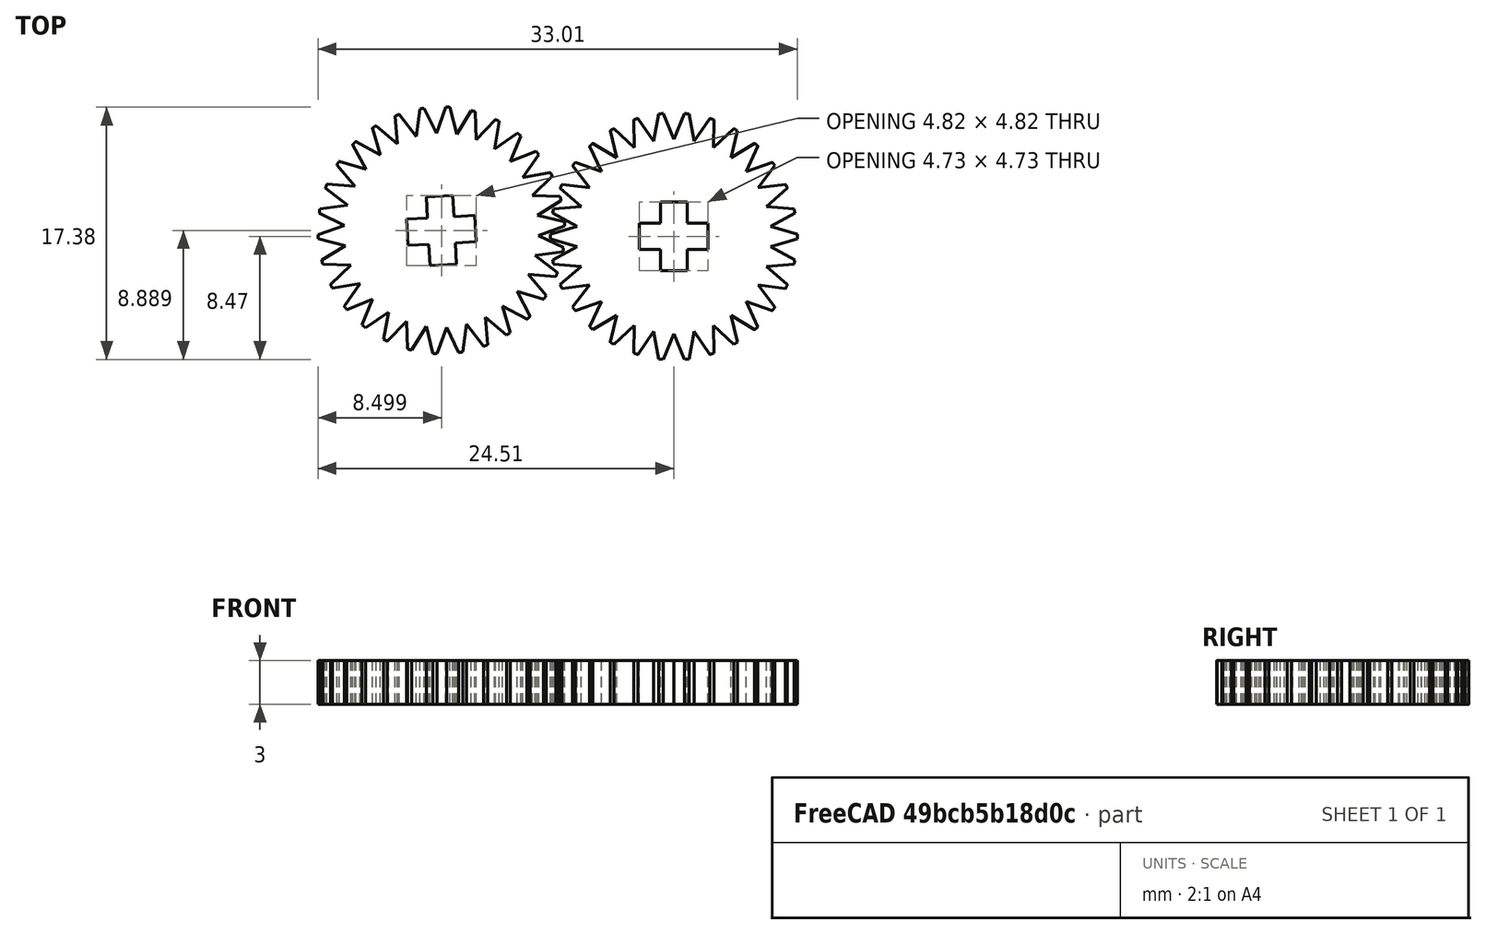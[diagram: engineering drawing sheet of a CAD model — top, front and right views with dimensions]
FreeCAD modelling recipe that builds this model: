
FCSTD DOCUMENT  (FreeCAD 0.18R16117 (Git))
Label: Gear
License: All rights reserved
LicenseURL: http://en.wikipedia.org/wiki/All_rights_reserved
objects: Sketcher::SketchObject×2, PartDesign::Pad×2, PartDesign::Body×2, Part::Cylinder×2, Part::MultiCommon×2
note: 12 computed .brp shape members not serialized (recipe doc carries the construction recipe); baked Part::Feature solids carry a one-line shape summary decoded from their .brp

FEATURE [Sketcher::SketchObject] Sketch
  MapMode = 5
  Support = -> [XY_Plane]
  sketch-geometry (72):
    g0: LineSegment StartX=0.940756 StartY=8.9507 StartZ=0 EndX=1.39301 EndY=6.55359 EndZ=0
    g1: LineSegment StartX=1.39301 StartY=6.55359 StartZ=0 EndX=2.78115 EndY=8.55951 EndZ=0
    g2: LineSegment StartX=2.78115 StartY=8.55951 StartZ=0 EndX=2.72514 EndY=6.12075 EndZ=0
    g3: LineSegment StartX=2.72514 StartY=6.12075 StartZ=0 EndX=4.5 EndY=7.79423 EndZ=0
    g4: LineSegment StartX=4.5 StartY=7.79423 StartZ=0 EndX=3.93816 EndY=5.42041 EndZ=0
    g5: LineSegment StartX=3.93816 StartY=5.42041 StartZ=0 EndX=6.02218 EndY=6.6883 EndZ=0
    g6: LineSegment StartX=6.02218 StartY=6.6883 StartZ=0 EndX=4.97907 EndY=4.48318 EndZ=0
    g7: LineSegment StartX=4.97907 StartY=4.48318 StartZ=0 EndX=7.28115 EndY=5.29007 EndZ=0
    g8: LineSegment StartX=7.28115 StartY=5.29007 StartZ=0 EndX=5.80237 EndY=3.35 EndZ=0
    g9: LineSegment StartX=5.80237 StartY=3.35 StartZ=0 EndX=8.22191 EndY=3.66063 EndZ=0
    g10: LineSegment StartX=8.22191 StartY=3.66063 StartZ=0 EndX=6.37208 EndY=2.07041 EndZ=0
    g11: LineSegment StartX=6.37208 StartY=2.07041 StartZ=0 EndX=8.80333 EndY=1.87121 EndZ=0
    g12: LineSegment StartX=8.80333 StartY=1.87121 StartZ=0 EndX=6.6633 EndY=0.700341 EndZ=0
    g13: LineSegment StartX=6.6633 StartY=0.700341 StartZ=0 EndX=9 EndY=0 EndZ=0
    g14: LineSegment StartX=9 StartY=0 StartZ=0 EndX=6.6633 EndY=-0.700341 EndZ=0
    g15: LineSegment StartX=6.6633 StartY=-0.700341 StartZ=0 EndX=8.80333 EndY=-1.87121 EndZ=0
    g16: LineSegment StartX=8.80333 StartY=-1.87121 StartZ=0 EndX=6.37208 EndY=-2.07041 EndZ=0
    g17: LineSegment StartX=6.37208 StartY=-2.07041 StartZ=0 EndX=8.22191 EndY=-3.66063 EndZ=0
    g18: LineSegment StartX=8.22191 StartY=-3.66063 StartZ=0 EndX=5.80237 EndY=-3.35 EndZ=0
    g19: LineSegment StartX=5.80237 StartY=-3.35 StartZ=0 EndX=7.28115 EndY=-5.29007 EndZ=0
    g20: LineSegment StartX=7.28115 StartY=-5.29007 StartZ=0 EndX=4.97907 EndY=-4.48318 EndZ=0
    g21: LineSegment StartX=4.97907 StartY=-4.48318 StartZ=0 EndX=6.02218 EndY=-6.6883 EndZ=0
    g22: LineSegment StartX=6.02218 StartY=-6.6883 StartZ=0 EndX=3.93816 EndY=-5.42041 EndZ=0
    g23: LineSegment StartX=3.93816 StartY=-5.42041 StartZ=0 EndX=4.5 EndY=-7.79423 EndZ=0
    g24: LineSegment StartX=4.5 StartY=-7.79423 StartZ=0 EndX=2.72514 EndY=-6.12075 EndZ=0
    g25: LineSegment StartX=2.72514 StartY=-6.12075 StartZ=0 EndX=2.78115 EndY=-8.55951 EndZ=0
    g26: LineSegment StartX=2.78115 StartY=-8.55951 StartZ=0 EndX=1.39301 EndY=-6.55359 EndZ=0
    g27: LineSegment StartX=1.39301 StartY=-6.55359 StartZ=0 EndX=0.940756 EndY=-8.9507 EndZ=0
    g28: LineSegment StartX=0.940756 StartY=-8.9507 StartZ=0 EndX=0 EndY=-6.7 EndZ=0
    g29: LineSegment StartX=0 StartY=-6.7 StartZ=0 EndX=-0.940756 EndY=-8.9507 EndZ=0
    g30: LineSegment StartX=-0.940756 StartY=-8.9507 StartZ=0 EndX=-1.39301 EndY=-6.55359 EndZ=0
    g31: LineSegment StartX=-1.39301 StartY=-6.55359 StartZ=0 EndX=-2.78115 EndY=-8.55951 EndZ=0
    g32: LineSegment StartX=-2.78115 StartY=-8.55951 StartZ=0 EndX=-2.72514 EndY=-6.12075 EndZ=0
    g33: LineSegment StartX=-2.72514 StartY=-6.12075 StartZ=0 EndX=-4.5 EndY=-7.79423 EndZ=0
    g34: LineSegment StartX=-4.5 StartY=-7.79423 StartZ=0 EndX=-3.93816 EndY=-5.42041 EndZ=0
    g35: LineSegment StartX=-3.93816 StartY=-5.42041 StartZ=0 EndX=-6.02218 EndY=-6.6883 EndZ=0
    g36: LineSegment StartX=-6.02218 StartY=-6.6883 StartZ=0 EndX=-4.97907 EndY=-4.48318 EndZ=0
    g37: LineSegment StartX=-4.97907 StartY=-4.48318 StartZ=0 EndX=-7.28115 EndY=-5.29007 EndZ=0
    g38: LineSegment StartX=-7.28115 StartY=-5.29007 StartZ=0 EndX=-5.80237 EndY=-3.35 EndZ=0
    g39: LineSegment StartX=-5.80237 StartY=-3.35 StartZ=0 EndX=-8.22191 EndY=-3.66063 EndZ=0
    g40: LineSegment StartX=-8.22191 StartY=-3.66063 StartZ=0 EndX=-6.37208 EndY=-2.07041 EndZ=0
    g41: LineSegment StartX=-6.37208 StartY=-2.07041 StartZ=0 EndX=-8.80333 EndY=-1.87121 EndZ=0
    g42: LineSegment StartX=-8.80333 StartY=-1.87121 StartZ=0 EndX=-6.6633 EndY=-0.700341 EndZ=0
    g43: LineSegment StartX=-6.6633 StartY=-0.700341 StartZ=0 EndX=-9 EndY=7e-15 EndZ=0
    g44: LineSegment StartX=-9 StartY=6.9e-15 StartZ=0 EndX=-6.6633 EndY=0.700341 EndZ=0
    g45: LineSegment StartX=-6.6633 StartY=0.700341 StartZ=0 EndX=-8.80333 EndY=1.87121 EndZ=0
    g46: LineSegment StartX=-8.80333 StartY=1.87121 StartZ=0 EndX=-6.37208 EndY=2.07041 EndZ=0
    g47: LineSegment StartX=-6.37208 StartY=2.07041 StartZ=0 EndX=-8.22191 EndY=3.66063 EndZ=0
    g48: LineSegment StartX=-8.22191 StartY=3.66063 StartZ=0 EndX=-5.80237 EndY=3.35 EndZ=0
    g49: LineSegment StartX=-5.80237 StartY=3.35 StartZ=0 EndX=-7.28115 EndY=5.29007 EndZ=0
    g50: LineSegment StartX=-7.28115 StartY=5.29007 StartZ=0 EndX=-4.97907 EndY=4.48318 EndZ=0
    g51: LineSegment StartX=-4.97907 StartY=4.48318 StartZ=0 EndX=-6.02218 EndY=6.6883 EndZ=0
    g52: LineSegment StartX=-6.02218 StartY=6.6883 StartZ=0 EndX=-3.93816 EndY=5.42041 EndZ=0
    g53: LineSegment StartX=-3.93816 StartY=5.42041 StartZ=0 EndX=-4.5 EndY=7.79423 EndZ=0
    g54: LineSegment StartX=-4.5 StartY=7.79423 StartZ=0 EndX=-2.72514 EndY=6.12075 EndZ=0
    g55: LineSegment StartX=-2.72514 StartY=6.12075 StartZ=0 EndX=-2.78115 EndY=8.55951 EndZ=0
    g56: LineSegment StartX=-2.78115 StartY=8.55951 StartZ=0 EndX=-1.39301 EndY=6.55359 EndZ=0
    g57: LineSegment StartX=-1.39301 StartY=6.55359 StartZ=0 EndX=-0.940756 EndY=8.9507 EndZ=0
    g58: LineSegment StartX=-0.940756 StartY=8.9507 StartZ=0 EndX=1.47e-14 EndY=6.7 EndZ=0
    g59: LineSegment StartX=1.47e-14 StartY=6.7 StartZ=0 EndX=0.940756 EndY=8.9507 EndZ=0
    g60: LineSegment StartX=-2.365 StartY=0.91 StartZ=0 EndX=-0.91 EndY=0.91 EndZ=0
    g61: LineSegment StartX=-0.91 StartY=0.91 StartZ=0 EndX=-0.91 EndY=2.365 EndZ=0
    g62: LineSegment StartX=-0.91 StartY=2.365 StartZ=0 EndX=0.91 EndY=2.365 EndZ=0
    g63: LineSegment StartX=0.91 StartY=2.365 StartZ=0 EndX=0.91 EndY=0.91 EndZ=0
    g64: LineSegment StartX=0.91 StartY=0.91 StartZ=0 EndX=2.365 EndY=0.91 EndZ=0
    g65: LineSegment StartX=2.365 StartY=0.91 StartZ=0 EndX=2.365 EndY=-0.91 EndZ=0
    g66: LineSegment StartX=2.365 StartY=-0.91 StartZ=0 EndX=0.91 EndY=-0.91 EndZ=0
    g67: LineSegment StartX=0.91 StartY=-0.91 StartZ=0 EndX=0.91 EndY=-2.365 EndZ=0
    g68: LineSegment StartX=0.91 StartY=-2.365 StartZ=0 EndX=-0.91 EndY=-2.365 EndZ=0
    g69: LineSegment StartX=-0.91 StartY=-2.365 StartZ=0 EndX=-0.91 EndY=-0.91 EndZ=0
    g70: LineSegment StartX=-0.91 StartY=-0.91 StartZ=0 EndX=-2.365 EndY=-0.91 EndZ=0
    g71: LineSegment StartX=-2.365 StartY=-0.91 StartZ=0 EndX=-2.365 EndY=0.91 EndZ=0
  constraints (96):
    c: Coincident(g0,g1)
    c: Coincident(g1,g2)
    c: Coincident(g2,g3)
    c: Coincident(g3,g4)
    c: Coincident(g4,g5)
    c: Coincident(g5,g6)
    c: Coincident(g6,g7)
    c: Coincident(g7,g8)
    c: Coincident(g8,g9)
    c: Coincident(g9,g10)
    c: Coincident(g10,g11)
    c: Coincident(g11,g12)
    c: Coincident(g12,g13)
    c: Coincident(g13,g14)
    c: Coincident(g14,g15)
    c: Coincident(g15,g16)
    c: Coincident(g16,g17)
    c: Coincident(g17,g18)
    c: Coincident(g18,g19)
    c: Coincident(g19,g20)
    c: Coincident(g20,g21)
    c: Coincident(g21,g22)
    c: Coincident(g22,g23)
    c: Coincident(g23,g24)
    c: Coincident(g24,g25)
    c: Coincident(g25,g26)
    c: Coincident(g26,g27)
    c: Coincident(g27,g28)
    c: Coincident(g28,g29)
    c: Coincident(g29,g30)
    c: Coincident(g30,g31)
    c: Coincident(g31,g32)
    c: Coincident(g32,g33)
    c: Coincident(g33,g34)
    c: Coincident(g34,g35)
    c: Coincident(g35,g36)
    c: Coincident(g36,g37)
    c: Coincident(g37,g38)
    c: Coincident(g38,g39)
    c: Coincident(g39,g40)
    c: Coincident(g40,g41)
    c: Coincident(g41,g42)
    c: Coincident(g42,g43)
    c: Coincident(g43,g44)
    c: Coincident(g44,g45)
    c: Coincident(g45,g46)
    c: Coincident(g46,g47)
    c: Coincident(g47,g48)
    c: Coincident(g48,g49)
    c: Coincident(g49,g50)
    c: Coincident(g50,g51)
    c: Coincident(g51,g52)
    c: Coincident(g52,g53)
    c: Coincident(g53,g54)
    c: Coincident(g54,g55)
    c: Coincident(g55,g56)
    c: Coincident(g56,g57)
    c: Coincident(g57,g58)
    c: Coincident(g58,g59)
    c: Coincident(g59,g0)
    c: Coincident(g60,g61)
    c: Coincident(g61,g62)
    c: Coincident(g62,g63)
    c: Coincident(g63,g64)
    c: Coincident(g64,g65)
    c: Coincident(g65,g66)
    c: Coincident(g66,g67)
    c: Coincident(g67,g68)
    c: Coincident(g68,g69)
    c: Coincident(g69,g70)
    c: Coincident(g70,g71)
    c: Coincident(g60,g71)
    c: Horizontal(g60)
    c: Horizontal(g62)
    c: Horizontal(g64)
    c: Horizontal(g66)
    c: Horizontal(g70)
    c: Vertical(g71)
    c: Vertical(g69)
    c: Vertical(g67)
    c: Vertical(g63)
    c: Vertical(g61)
    c: Equal(g60,g70)
    c: Equal(g70,g61)
    c: Equal(g61,g63)
    c: Equal(g63,g64)
    c: Equal(g64,g66)
    c: Equal(g66,g69)
    c: Equal(g69,g67)
    c: Equal(g62,g65)
    c: Equal(g65,g68)
    c: Equal(g68,g71)
    c: Distance(g65) = 1.82
    c: Distance(g62,g68) = 4.73
    c: DistanceX(g-2,g63) = 0.91
    c: DistanceY(g-1,g66) = -0.91
FEATURE [PartDesign::Pad] Pad
  Length = 3
  Length2 = 100
  Profile = -> Sketch
  Type = 0
FEATURE [PartDesign::Body] Body
  Group = -> [Sketch,Pad]
  Origin = -> Origin
  Placement = pos=(8,0,0) rot=(0,0,1;0rad)
  Tip = -> Pad
FEATURE [Part::Cylinder] Cylinder
  Angle = 360
  AttacherType = Attacher::AttachEngine3D
  Height = 10
  Placement = pos=(8,0,-3.5) rot=(0,0,1;0rad)
  Radius = 8.5
FEATURE [Part::MultiCommon] Common
  Shapes = -> [Cylinder,Body]
FEATURE [Sketcher::SketchObject] Sketch001
  MapMode = 5
  Support = -> [XY_Plane001]
  sketch-geometry (72):
    g0: LineSegment StartX=0.940756 StartY=8.9507 StartZ=0 EndX=1.39301 EndY=6.55359 EndZ=0
    g1: LineSegment StartX=1.39301 StartY=6.55359 StartZ=0 EndX=2.78115 EndY=8.55951 EndZ=0
    g2: LineSegment StartX=2.78115 StartY=8.55951 StartZ=0 EndX=2.72514 EndY=6.12075 EndZ=0
    g3: LineSegment StartX=2.72514 StartY=6.12075 StartZ=0 EndX=4.5 EndY=7.79423 EndZ=0
    g4: LineSegment StartX=4.5 StartY=7.79423 StartZ=0 EndX=3.93816 EndY=5.42041 EndZ=0
    g5: LineSegment StartX=3.93816 StartY=5.42041 StartZ=0 EndX=6.02218 EndY=6.6883 EndZ=0
    g6: LineSegment StartX=6.02218 StartY=6.6883 StartZ=0 EndX=4.97907 EndY=4.48318 EndZ=0
    g7: LineSegment StartX=4.97907 StartY=4.48318 StartZ=0 EndX=7.28115 EndY=5.29007 EndZ=0
    g8: LineSegment StartX=7.28115 StartY=5.29007 StartZ=0 EndX=5.80237 EndY=3.35 EndZ=0
    g9: LineSegment StartX=5.80237 StartY=3.35 StartZ=0 EndX=8.22191 EndY=3.66063 EndZ=0
    g10: LineSegment StartX=8.22191 StartY=3.66063 StartZ=0 EndX=6.37208 EndY=2.07041 EndZ=0
    g11: LineSegment StartX=6.37208 StartY=2.07041 StartZ=0 EndX=8.80333 EndY=1.87121 EndZ=0
    g12: LineSegment StartX=8.80333 StartY=1.87121 StartZ=0 EndX=6.6633 EndY=0.700341 EndZ=0
    g13: LineSegment StartX=6.6633 StartY=0.700341 StartZ=0 EndX=9 EndY=0 EndZ=0
    g14: LineSegment StartX=9 StartY=0 StartZ=0 EndX=6.6633 EndY=-0.700341 EndZ=0
    g15: LineSegment StartX=6.6633 StartY=-0.700341 StartZ=0 EndX=8.80333 EndY=-1.87121 EndZ=0
    g16: LineSegment StartX=8.80333 StartY=-1.87121 StartZ=0 EndX=6.37208 EndY=-2.07041 EndZ=0
    g17: LineSegment StartX=6.37208 StartY=-2.07041 StartZ=0 EndX=8.22191 EndY=-3.66063 EndZ=0
    g18: LineSegment StartX=8.22191 StartY=-3.66063 StartZ=0 EndX=5.80237 EndY=-3.35 EndZ=0
    g19: LineSegment StartX=5.80237 StartY=-3.35 StartZ=0 EndX=7.28115 EndY=-5.29007 EndZ=0
    g20: LineSegment StartX=7.28115 StartY=-5.29007 StartZ=0 EndX=4.97907 EndY=-4.48318 EndZ=0
    g21: LineSegment StartX=4.97907 StartY=-4.48318 StartZ=0 EndX=6.02218 EndY=-6.6883 EndZ=0
    g22: LineSegment StartX=6.02218 StartY=-6.6883 StartZ=0 EndX=3.93816 EndY=-5.42041 EndZ=0
    g23: LineSegment StartX=3.93816 StartY=-5.42041 StartZ=0 EndX=4.5 EndY=-7.79423 EndZ=0
    g24: LineSegment StartX=4.5 StartY=-7.79423 StartZ=0 EndX=2.72514 EndY=-6.12075 EndZ=0
    g25: LineSegment StartX=2.72514 StartY=-6.12075 StartZ=0 EndX=2.78115 EndY=-8.55951 EndZ=0
    g26: LineSegment StartX=2.78115 StartY=-8.55951 StartZ=0 EndX=1.39301 EndY=-6.55359 EndZ=0
    g27: LineSegment StartX=1.39301 StartY=-6.55359 StartZ=0 EndX=0.940756 EndY=-8.9507 EndZ=0
    g28: LineSegment StartX=0.940756 StartY=-8.9507 StartZ=0 EndX=0 EndY=-6.7 EndZ=0
    g29: LineSegment StartX=0 StartY=-6.7 StartZ=0 EndX=-0.940756 EndY=-8.9507 EndZ=0
    g30: LineSegment StartX=-0.940756 StartY=-8.9507 StartZ=0 EndX=-1.39301 EndY=-6.55359 EndZ=0
    g31: LineSegment StartX=-1.39301 StartY=-6.55359 StartZ=0 EndX=-2.78115 EndY=-8.55951 EndZ=0
    g32: LineSegment StartX=-2.78115 StartY=-8.55951 StartZ=0 EndX=-2.72514 EndY=-6.12075 EndZ=0
    g33: LineSegment StartX=-2.72514 StartY=-6.12075 StartZ=0 EndX=-4.5 EndY=-7.79423 EndZ=0
    g34: LineSegment StartX=-4.5 StartY=-7.79423 StartZ=0 EndX=-3.93816 EndY=-5.42041 EndZ=0
    g35: LineSegment StartX=-3.93816 StartY=-5.42041 StartZ=0 EndX=-6.02218 EndY=-6.6883 EndZ=0
    g36: LineSegment StartX=-6.02218 StartY=-6.6883 StartZ=0 EndX=-4.97907 EndY=-4.48318 EndZ=0
    g37: LineSegment StartX=-4.97907 StartY=-4.48318 StartZ=0 EndX=-7.28115 EndY=-5.29007 EndZ=0
    g38: LineSegment StartX=-7.28115 StartY=-5.29007 StartZ=0 EndX=-5.80237 EndY=-3.35 EndZ=0
    g39: LineSegment StartX=-5.80237 StartY=-3.35 StartZ=0 EndX=-8.22191 EndY=-3.66063 EndZ=0
    g40: LineSegment StartX=-8.22191 StartY=-3.66063 StartZ=0 EndX=-6.37208 EndY=-2.07041 EndZ=0
    g41: LineSegment StartX=-6.37208 StartY=-2.07041 StartZ=0 EndX=-8.80333 EndY=-1.87121 EndZ=0
    g42: LineSegment StartX=-8.80333 StartY=-1.87121 StartZ=0 EndX=-6.6633 EndY=-0.700341 EndZ=0
    g43: LineSegment StartX=-6.6633 StartY=-0.700341 StartZ=0 EndX=-9 EndY=6.9e-15 EndZ=0
    g44: LineSegment StartX=-9 StartY=6.9e-15 StartZ=0 EndX=-6.6633 EndY=0.700341 EndZ=0
    g45: LineSegment StartX=-6.6633 StartY=0.700341 StartZ=0 EndX=-8.80333 EndY=1.87121 EndZ=0
    g46: LineSegment StartX=-8.80333 StartY=1.87121 StartZ=0 EndX=-6.37208 EndY=2.07041 EndZ=0
    g47: LineSegment StartX=-6.37208 StartY=2.07041 StartZ=0 EndX=-8.22191 EndY=3.66063 EndZ=0
    g48: LineSegment StartX=-8.22191 StartY=3.66063 StartZ=0 EndX=-5.80237 EndY=3.35 EndZ=0
    g49: LineSegment StartX=-5.80237 StartY=3.35 StartZ=0 EndX=-7.28115 EndY=5.29007 EndZ=0
    g50: LineSegment StartX=-7.28115 StartY=5.29007 StartZ=0 EndX=-4.97907 EndY=4.48318 EndZ=0
    g51: LineSegment StartX=-4.97907 StartY=4.48318 StartZ=0 EndX=-6.02218 EndY=6.6883 EndZ=0
    g52: LineSegment StartX=-6.02218 StartY=6.6883 StartZ=0 EndX=-3.93816 EndY=5.42041 EndZ=0
    g53: LineSegment StartX=-3.93816 StartY=5.42041 StartZ=0 EndX=-4.5 EndY=7.79423 EndZ=0
    g54: LineSegment StartX=-4.5 StartY=7.79423 StartZ=0 EndX=-2.72514 EndY=6.12075 EndZ=0
    g55: LineSegment StartX=-2.72514 StartY=6.12075 StartZ=0 EndX=-2.78115 EndY=8.55951 EndZ=0
    g56: LineSegment StartX=-2.78115 StartY=8.55951 StartZ=0 EndX=-1.39301 EndY=6.55359 EndZ=0
    g57: LineSegment StartX=-1.39301 StartY=6.55359 StartZ=0 EndX=-0.940756 EndY=8.9507 EndZ=0
    g58: LineSegment StartX=-0.940756 StartY=8.9507 StartZ=0 EndX=1.47e-14 EndY=6.7 EndZ=0
    g59: LineSegment StartX=1.47e-14 StartY=6.7 StartZ=0 EndX=0.940756 EndY=8.9507 EndZ=0
    g60: LineSegment StartX=-2.365 StartY=0.91 StartZ=0 EndX=-0.91 EndY=0.91 EndZ=0
    g61: LineSegment StartX=-0.91 StartY=0.91 StartZ=0 EndX=-0.91 EndY=2.365 EndZ=0
    g62: LineSegment StartX=-0.91 StartY=2.365 StartZ=0 EndX=0.91 EndY=2.365 EndZ=0
    g63: LineSegment StartX=0.91 StartY=2.365 StartZ=0 EndX=0.91 EndY=0.91 EndZ=0
    g64: LineSegment StartX=0.91 StartY=0.91 StartZ=0 EndX=2.365 EndY=0.91 EndZ=0
    g65: LineSegment StartX=2.365 StartY=0.91 StartZ=0 EndX=2.365 EndY=-0.91 EndZ=0
    g66: LineSegment StartX=2.365 StartY=-0.91 StartZ=0 EndX=0.91 EndY=-0.91 EndZ=0
    g67: LineSegment StartX=0.91 StartY=-0.91 StartZ=0 EndX=0.91 EndY=-2.365 EndZ=0
    g68: LineSegment StartX=0.91 StartY=-2.365 StartZ=0 EndX=-0.91 EndY=-2.365 EndZ=0
    g69: LineSegment StartX=-0.91 StartY=-2.365 StartZ=0 EndX=-0.91 EndY=-0.91 EndZ=0
    g70: LineSegment StartX=-0.91 StartY=-0.91 StartZ=0 EndX=-2.365 EndY=-0.91 EndZ=0
    g71: LineSegment StartX=-2.365 StartY=-0.91 StartZ=0 EndX=-2.365 EndY=0.91 EndZ=0
  constraints (96):
    c: Coincident(g0,g1)
    c: Coincident(g1,g2)
    c: Coincident(g2,g3)
    c: Coincident(g3,g4)
    c: Coincident(g4,g5)
    c: Coincident(g5,g6)
    c: Coincident(g6,g7)
    c: Coincident(g7,g8)
    c: Coincident(g8,g9)
    c: Coincident(g9,g10)
    c: Coincident(g10,g11)
    c: Coincident(g11,g12)
    c: Coincident(g12,g13)
    c: Coincident(g13,g14)
    c: Coincident(g14,g15)
    c: Coincident(g15,g16)
    c: Coincident(g16,g17)
    c: Coincident(g17,g18)
    c: Coincident(g18,g19)
    c: Coincident(g19,g20)
    c: Coincident(g20,g21)
    c: Coincident(g21,g22)
    c: Coincident(g22,g23)
    c: Coincident(g23,g24)
    c: Coincident(g24,g25)
    c: Coincident(g25,g26)
    c: Coincident(g26,g27)
    c: Coincident(g27,g28)
    c: Coincident(g28,g29)
    c: Coincident(g29,g30)
    c: Coincident(g30,g31)
    c: Coincident(g31,g32)
    c: Coincident(g32,g33)
    c: Coincident(g33,g34)
    c: Coincident(g34,g35)
    c: Coincident(g35,g36)
    c: Coincident(g36,g37)
    c: Coincident(g37,g38)
    c: Coincident(g38,g39)
    c: Coincident(g39,g40)
    c: Coincident(g40,g41)
    c: Coincident(g41,g42)
    c: Coincident(g42,g43)
    c: Coincident(g43,g44)
    c: Coincident(g44,g45)
    c: Coincident(g45,g46)
    c: Coincident(g46,g47)
    c: Coincident(g47,g48)
    c: Coincident(g48,g49)
    c: Coincident(g49,g50)
    c: Coincident(g50,g51)
    c: Coincident(g51,g52)
    c: Coincident(g52,g53)
    c: Coincident(g53,g54)
    c: Coincident(g54,g55)
    c: Coincident(g55,g56)
    c: Coincident(g56,g57)
    c: Coincident(g57,g58)
    c: Coincident(g58,g59)
    c: Coincident(g59,g0)
    c: Coincident(g60,g61)
    c: Coincident(g61,g62)
    c: Coincident(g62,g63)
    c: Coincident(g63,g64)
    c: Coincident(g64,g65)
    c: Coincident(g65,g66)
    c: Coincident(g66,g67)
    c: Coincident(g67,g68)
    c: Coincident(g68,g69)
    c: Coincident(g69,g70)
    c: Coincident(g70,g71)
    c: Coincident(g60,g71)
    c: Horizontal(g60)
    c: Horizontal(g62)
    c: Horizontal(g64)
    c: Horizontal(g66)
    c: Horizontal(g70)
    c: Vertical(g71)
    c: Vertical(g69)
    c: Vertical(g67)
    c: Vertical(g63)
    c: Vertical(g61)
    c: Equal(g60,g70)
    c: Equal(g70,g61)
    c: Equal(g61,g63)
    c: Equal(g63,g64)
    c: Equal(g64,g66)
    c: Equal(g66,g69)
    c: Equal(g69,g67)
    c: Equal(g62,g65)
    c: Equal(g65,g68)
    c: Equal(g68,g71)
    c: Distance(g65) = 1.82
    c: Distance(g62,g68) = 4.73
    c: DistanceX(g-2,g63) = 0.91
    c: DistanceY(g-1,g66) = -0.91
FEATURE [PartDesign::Pad] Pad001
  Length = 3
  Length2 = 100
  Profile = -> Sketch001
  Type = 0
FEATURE [Part::Cylinder] Cylinder001
  Angle = 360
  AttacherType = Attacher::AttachEngine3D
  Height = 10
  Placement = pos=(8,0,-3.5) rot=(0,0,1;0rad)
  Radius = 8.5
FEATURE [PartDesign::Body] Body001
  Group = -> [Sketch001,Pad001]
  Origin = -> Origin001
  Placement = pos=(8,0,0) rot=(0,0,1;0rad)
  Tip = -> Pad001
FEATURE [Part::MultiCommon] Common001
  Placement = pos=(-16,0,0) rot=(0,0,1;0.05236rad)
  Shapes = -> [Cylinder001,Body001]
